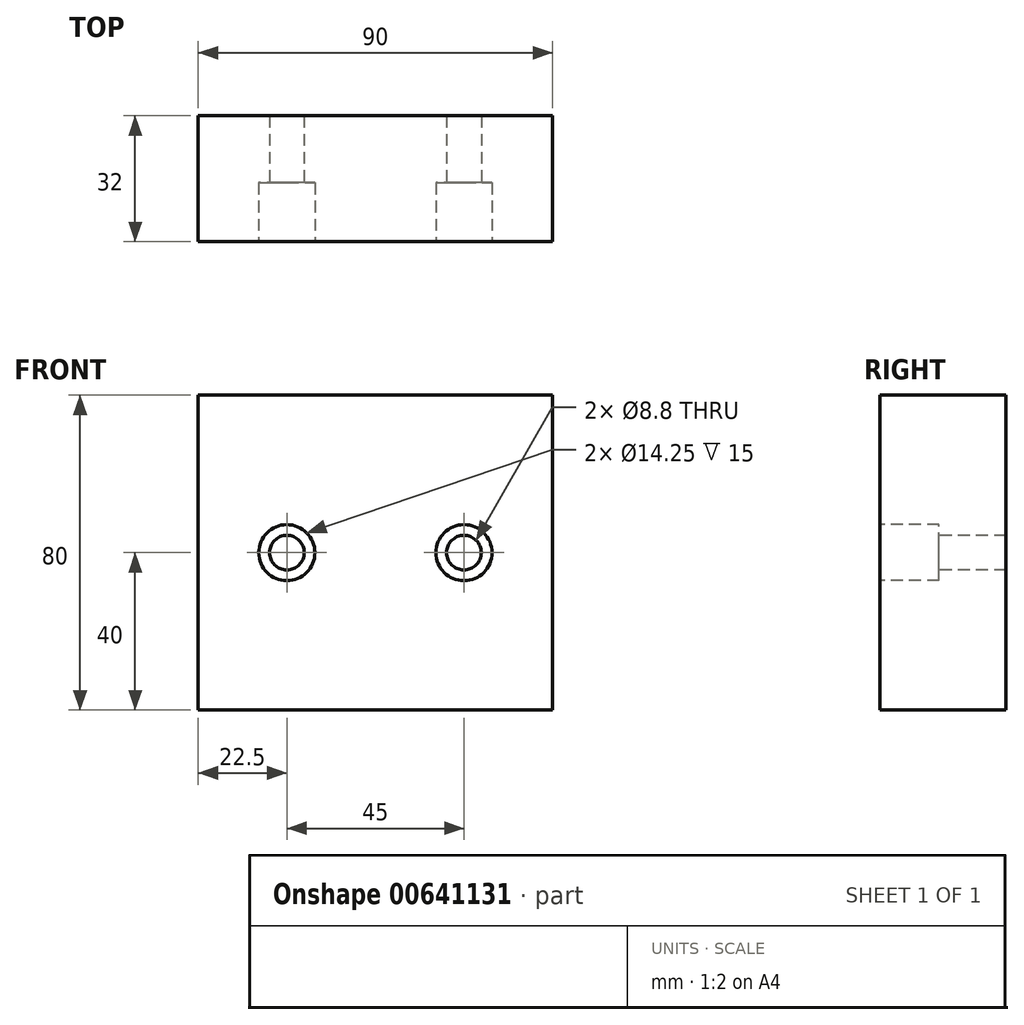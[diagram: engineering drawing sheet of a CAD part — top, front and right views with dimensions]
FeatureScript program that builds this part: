
annotation { "Feature Type Name" : "Feature", "Feature Type Description" : "" }
export const myFeature = defineFeature(function(context is Context, id is Id, definition is map)
    precondition{}
    {
        {
            var Q0;
            Q0=qCreatedBy(makeId("Front.planeOp"),FACE);
            var sketch = newSketch(context, id + "F0", { "sketchPlane" : qUnion([Q0])});
            skLineSegment(sketch, "E0.bottom", {"start": v(0, 0) * mm, "end": v(90, 0) * mm});
            skLineSegment(sketch, "E0.top", {"start": v(0, 80) * mm, "end": v(90, 80) * mm});
            skLineSegment(sketch, "E0.left", {"start": v(0, 0) * mm, "end": v(0, 80) * mm});
            skLineSegment(sketch, "E0.right", {"start": v(90, 0) * mm, "end": v(90, 80) * mm});
            skSolve(sketch);
        }
        {
            var Q0;
            Q0 = qSketchRegion(id + "F0", true);
            var Q1;
            Q1=makeQuery(id+"F0.imprint","IMPRINT",FACE,{"disambiguationData":[TD([[makeQuery(id+"F0.imprint","IMPRINT",EDGE,{"derivedFrom":sQuery(id+"F0.wireOp",EDGE,"E0.bottom")}),1.0]])]});
            extrude(context, id + "F1", {"entities" : qUnion([Q0, Q1]), "depth" : 32 * mm, "offsetDistance" : 25 * mm});
        }
        {
            var Q0;
            Q0=makeQuery(id+"F1.opExtrude","CAP_FACE",FACE,{"disambiguationData":[OSD([sQuery(id+"F0.wireOp",EDGE,"E0.bottom"),sQuery(id+"F0.wireOp",EDGE,"E0.top"),sQuery(id+"F0.wireOp",EDGE,"E0.left"),sQuery(id+"F0.wireOp",EDGE,"E0.right")])],"isStart":false});
            var sketch = newSketch(context, id + "F2", { "sketchPlane" : qUnion([Q0])});
            skPoint(sketch, "E1", {"position": v(0, 40) * mm});
            skPoint(sketch, "E2", {"position": v(22.5, 40) * mm});
            skPoint(sketch, "E3", {"position": v(67.5, 40) * mm});
            skSolve(sketch);
        }
        {
            var Q0;
            Q0=sQuery(id+"F2.wireOp",VERTEX,"E2");
            var Q1;
            Q1=sQuery(id+"F2.wireOp",VERTEX,"E3");
            var Q2;
            Q2=makeQuery(id+"F1.opExtrude","SWEPT_BODY",BODY,{"disambiguationData":[OSD([sQuery(id+"F0.wireOp",EDGE,"E0.bottom"),sQuery(id+"F0.wireOp",EDGE,"E0.top"),sQuery(id+"F0.wireOp",EDGE,"E0.left"),sQuery(id+"F0.wireOp",EDGE,"E0.right")])]});
            hole(context, id + "F3", {"style" : HoleStyle.C_BORE, "endStyle" : HoleEndStyle.THROUGH, "holeDiameter" : 8.8 * mm, "cBoreDiameter" : 14.25 * mm, "cBoreDepth" : 15 * mm, "majorDiameter" : 8 * mm, "isTappedThrough" : true, "tappedDepth" : 14.5 * mm, "tapClearance" : 3, "startFromSketch" : true, "locations" : qUnion([Q0, Q1]), "scope" : qUnion([Q2])});
        }
    });
